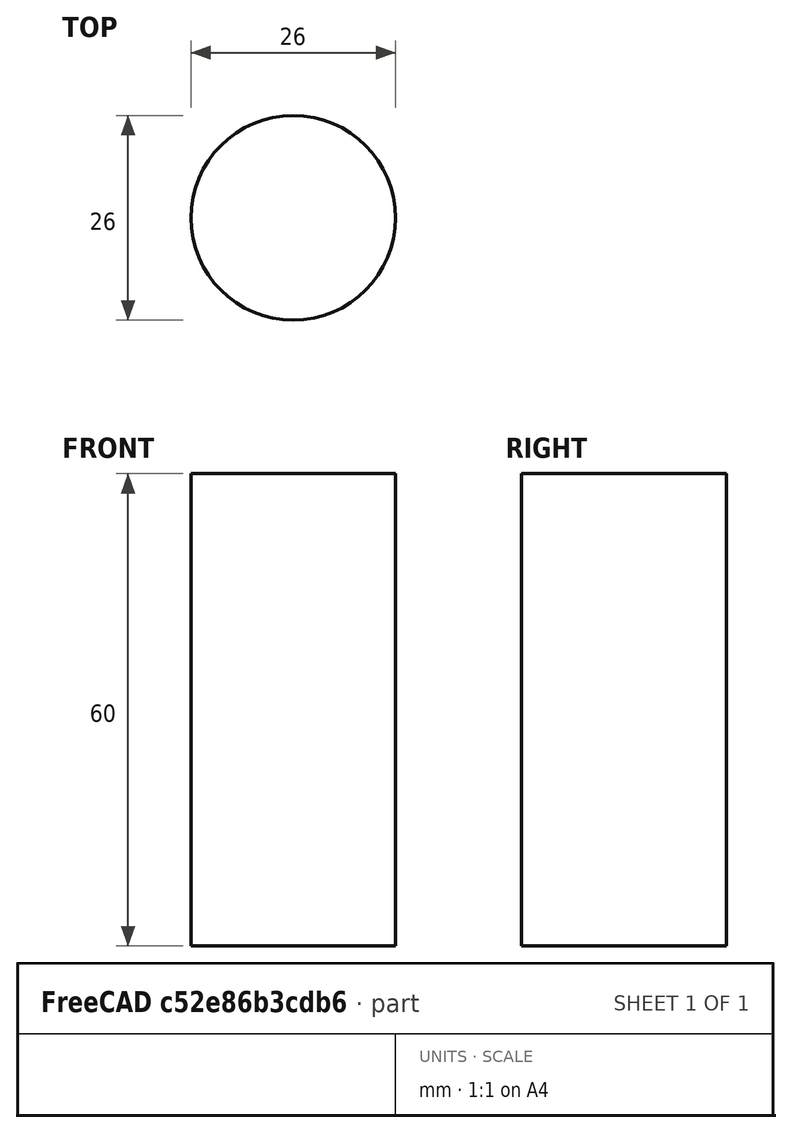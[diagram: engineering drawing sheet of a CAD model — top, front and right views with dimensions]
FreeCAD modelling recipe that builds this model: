
FCSTD DOCUMENT  (FreeCAD 0.19R24267 +148 (Git))
Label: IntestineV5_outer_collision
License: All rights reserved
LicenseURL: http://en.wikipedia.org/wiki/All_rights_reserved
objects: Sketcher::SketchObject×1, Part::Revolution×1, Part::Reverse×1
note: 3 computed .brp shape members not serialized (recipe doc carries the construction recipe); baked Part::Feature solids carry a one-line shape summary decoded from their .brp

FEATURE [Sketcher::SketchObject] Sketch
  FullyConstrained = true
  Placement = pos=(0,0,0) rot=(1,0,0;1.5708rad)
  sketch-geometry (1):
    g0: LineSegment StartX=13 StartY=60 StartZ=0 EndX=13 EndY=0 EndZ=0
  constraints (4):
    c: Vertical(g0)
    c: DistanceX(g-1,g0) = 13
    c: DistanceY(g0,g-1) = 0
    c: DistanceY(g0,g0) = 60
FEATURE [Part::Revolution] Revolve
  Angle = 360
  Axis = (0,0,1)
  Base = (0,0,0)
  FaceMakerClass = Part::FaceMakerBullseye
  Solid = false
  Source = -> Sketch
  Symmetric = false
FEATURE [Part::Reverse] Revolve_rev  label="Revolve (Rev)"
  Source = -> Revolve
